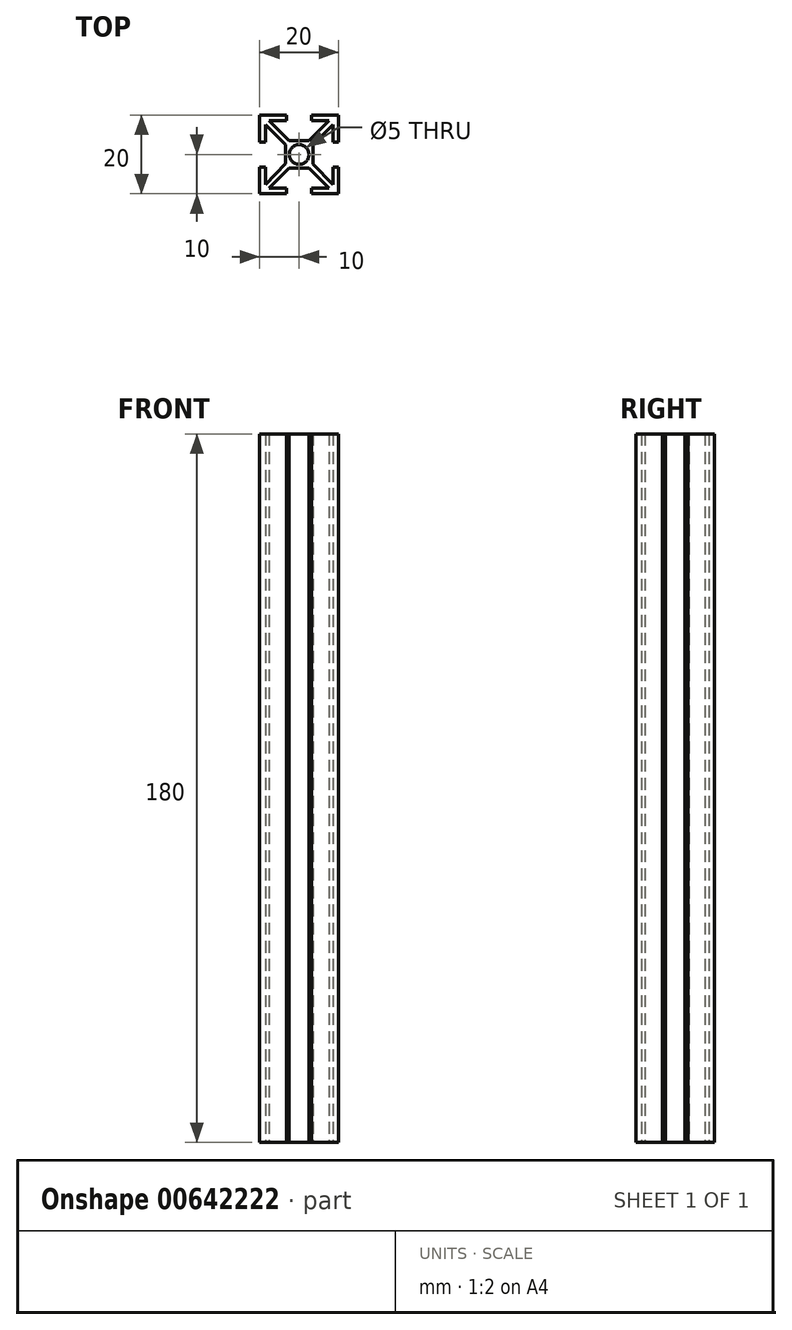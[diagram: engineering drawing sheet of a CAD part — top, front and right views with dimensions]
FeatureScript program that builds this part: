
annotation { "Feature Type Name" : "Feature", "Feature Type Description" : "" }
export const myFeature = defineFeature(function(context is Context, id is Id, definition is map)
    precondition{}
    {
        {
            var Q0;
            Q0=qCreatedBy(makeId("Top.planeOp"),FACE);
            var sketch = newSketch(context, id + "F0", { "sketchPlane" : qUnion([Q0])});
            skCircle(sketch, "E0", {"center": v(10, 10) * mm, "radius": 2.5 * mm});
            skLineSegment(sketch, "E1", {"start": v(0, 0) * mm, "end": v(10, 10) * mm, "construction": true});
            skLineSegment(sketch, "E2", {"start": v(1.4, 2.39) * mm, "end": v(1.4, 6.8) * mm});
            skLineSegment(sketch, "E3", {"start": v(1.4, 6.8) * mm, "end": v(0, 6.8) * mm});
            skLineSegment(sketch, "E4", {"start": v(0, 6.8) * mm, "end": v(0, 0) * mm});
            skLineSegment(sketch, "E5", {"start": v(7.49, 6.5) * mm, "end": v(2.39, 1.4) * mm});
            skLineSegment(sketch, "E6", {"start": v(2.39, 1.4) * mm, "end": v(6.8, 1.4) * mm});
            skLineSegment(sketch, "E7", {"start": v(6.8, 1.4) * mm, "end": v(6.8, 0) * mm});
            skLineSegment(sketch, "E8", {"start": v(6.8, 0) * mm, "end": v(0, 0) * mm});
            skLineSegment(sketch, "E9", {"start": v(10, 10) * mm, "end": v(20, 20) * mm, "construction": true});
            skLineSegment(sketch, "E10", {"start": v(10, 10) * mm, "end": v(0, 20) * mm, "construction": true});
            skLineSegment(sketch, "E11", {"start": v(10, 10) * mm, "end": v(20, 0) * mm, "construction": true});
            skLineSegment(sketch, "E12", {"start": v(1.4, 17.61) * mm, "end": v(6.5, 12.51) * mm});
            skLineSegment(sketch, "E13", {"start": v(1.4, 17.61) * mm, "end": v(1.4, 13.2) * mm});
            skLineSegment(sketch, "E14", {"start": v(1.4, 13.2) * mm, "end": v(0, 13.2) * mm});
            skLineSegment(sketch, "E15", {"start": v(0, 13.2) * mm, "end": v(0, 20) * mm});
            skLineSegment(sketch, "E16", {"start": v(7.49, 13.5) * mm, "end": v(2.39, 18.6) * mm});
            skLineSegment(sketch, "E17", {"start": v(2.39, 18.6) * mm, "end": v(6.8, 18.6) * mm});
            skLineSegment(sketch, "E18", {"start": v(6.8, 18.6) * mm, "end": v(6.8, 20) * mm});
            skLineSegment(sketch, "E19", {"start": v(6.8, 20) * mm, "end": v(0, 20) * mm});
            skLineSegment(sketch, "E20", {"start": v(12.51, 13.5) * mm, "end": v(17.61, 18.6) * mm});
            skLineSegment(sketch, "E21", {"start": v(17.61, 18.6) * mm, "end": v(13.2, 18.6) * mm});
            skLineSegment(sketch, "E22", {"start": v(13.2, 18.6) * mm, "end": v(13.2, 20) * mm});
            skLineSegment(sketch, "E23", {"start": v(13.2, 20) * mm, "end": v(20, 20) * mm});
            skLineSegment(sketch, "E24", {"start": v(13.5, 12.51) * mm, "end": v(18.6, 17.61) * mm});
            skLineSegment(sketch, "E25", {"start": v(18.6, 17.61) * mm, "end": v(18.6, 13.2) * mm});
            skLineSegment(sketch, "E26", {"start": v(18.6, 13.2) * mm, "end": v(20, 13.2) * mm});
            skLineSegment(sketch, "E27", {"start": v(20, 13.2) * mm, "end": v(20, 20) * mm});
            skLineSegment(sketch, "E28", {"start": v(18.6, 2.39) * mm, "end": v(18.6, 6.8) * mm});
            skLineSegment(sketch, "E29", {"start": v(18.6, 6.8) * mm, "end": v(20, 6.8) * mm});
            skLineSegment(sketch, "E30", {"start": v(20, 6.8) * mm, "end": v(20, 0) * mm});
            skLineSegment(sketch, "E31", {"start": v(12.51, 6.5) * mm, "end": v(17.61, 1.4) * mm});
            skLineSegment(sketch, "E32", {"start": v(17.61, 1.4) * mm, "end": v(13.2, 1.4) * mm});
            skLineSegment(sketch, "E33", {"start": v(13.2, 1.4) * mm, "end": v(13.2, 0) * mm});
            skLineSegment(sketch, "E34", {"start": v(13.2, 0) * mm, "end": v(20, 0) * mm});
            skLineSegment(sketch, "E35", {"start": v(12.51, 6.5) * mm, "end": v(7.49, 6.5) * mm});
            skLineSegment(sketch, "E36", {"start": v(7.49, 13.5) * mm, "end": v(12.51, 13.5) * mm});
            skLineSegment(sketch, "E37", {"start": v(10, 10) * mm, "end": v(10, 0) * mm, "construction": true});
            skLineSegment(sketch, "E38", {"start": v(10, 10) * mm, "end": v(18.77, 10) * mm, "construction": true});
            skLineSegment(sketch, "E39", {"start": v(10, 10) * mm, "end": v(10, 20.74) * mm, "construction": true});
            skLineSegment(sketch, "E40", {"start": v(10, 10) * mm, "end": v(0, 10) * mm, "construction": true});
            skLineSegment(sketch, "E41.bottom", {"start": v(0, 0) * mm, "end": v(20, 0) * mm, "construction": true});
            skLineSegment(sketch, "E41.top", {"start": v(0, 20) * mm, "end": v(20, 20) * mm, "construction": true});
            skLineSegment(sketch, "E41.left", {"start": v(0, 0) * mm, "end": v(0, 20) * mm, "construction": true});
            skLineSegment(sketch, "E41.right", {"start": v(20, 0) * mm, "end": v(20, 20) * mm, "construction": true});
            skLineSegment(sketch, "E42", {"start": v(18.6, 2.39) * mm, "end": v(13.5, 7.49) * mm});
            skLineSegment(sketch, "E43", {"start": v(13.5, 7.49) * mm, "end": v(13.5, 12.51) * mm});
            skLineSegment(sketch, "E44", {"start": v(1.4, 2.39) * mm, "end": v(6.5, 7.62) * mm});
            skLineSegment(sketch, "E45", {"start": v(6.5, 7.62) * mm, "end": v(6.5, 12.51) * mm});
            skSolve(sketch);
        }
        {
            var Q0;
            Q0=makeQuery(id+"F0.imprint","IMPRINT",FACE,{"disambiguationData":[TD([[makeQuery(id+"F0.imprint","IMPRINT",EDGE,{"derivedFrom":sQuery(id+"F0.wireOp",EDGE,"E0")}),-1.0]])]});
            extrude(context, id + "F1", {"entities" : qUnion([Q0]), "depth" : 180 * mm, "offsetDistance" : 25 * mm});
        }
    });
